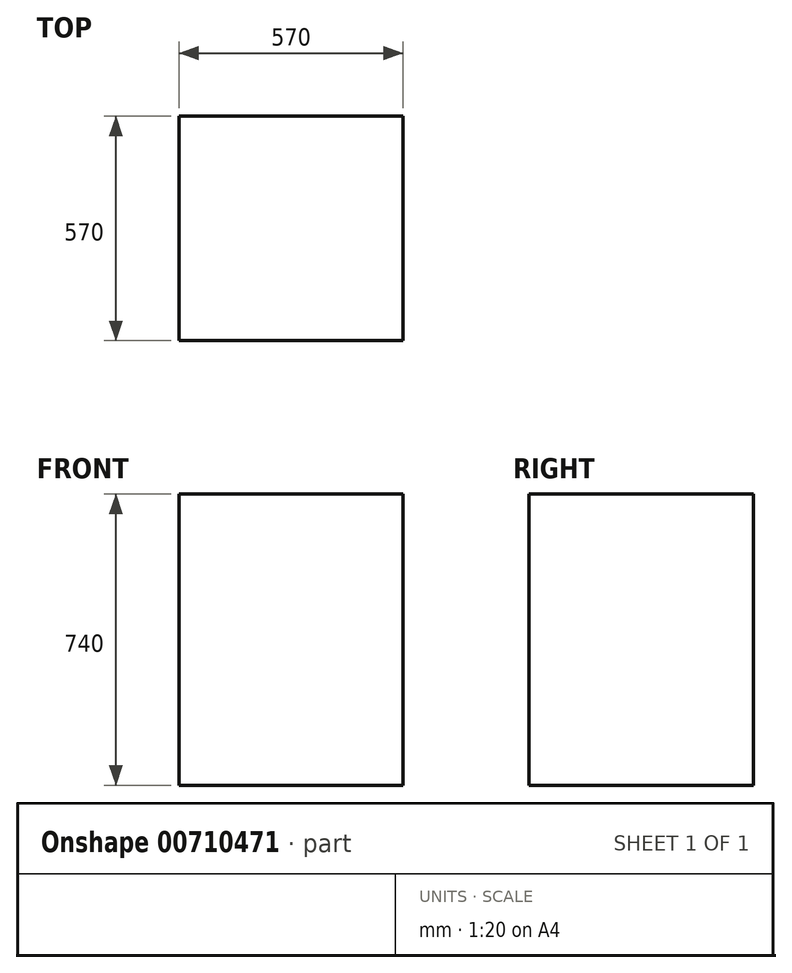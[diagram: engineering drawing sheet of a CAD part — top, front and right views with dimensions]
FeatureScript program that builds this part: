
annotation { "Feature Type Name" : "Feature", "Feature Type Description" : "" }
export const myFeature = defineFeature(function(context is Context, id is Id, definition is map)
    precondition{}
    {
        {
            var Q0;
            Q0=qCreatedBy(makeId("Top.planeOp"),FACE);
            var sketch = newSketch(context, id + "F0", { "sketchPlane" : qUnion([Q0])});
            skLineSegment(sketch, "E0.bottom", {"start": v(285, 285) * mm, "end": v(-285, 285) * mm});
            skLineSegment(sketch, "E0.top", {"start": v(285, -285) * mm, "end": v(-285, -285) * mm});
            skLineSegment(sketch, "E0.left", {"start": v(285, 285) * mm, "end": v(285, -285) * mm});
            skLineSegment(sketch, "E0.right", {"start": v(-285, 285) * mm, "end": v(-285, -285) * mm});
            skPoint(sketch, "E0.middle", {"position": v(0, 0) * mm});
            skSolve(sketch);
        }
        {
            var Q0;
            Q0 = qSketchRegion(id + "F0", true);
            extrude(context, id + "F1", {"entities" : qUnion([Q0]), "depth" : 740 * mm, "offsetDistance" : 25 * mm});
        }
    });
